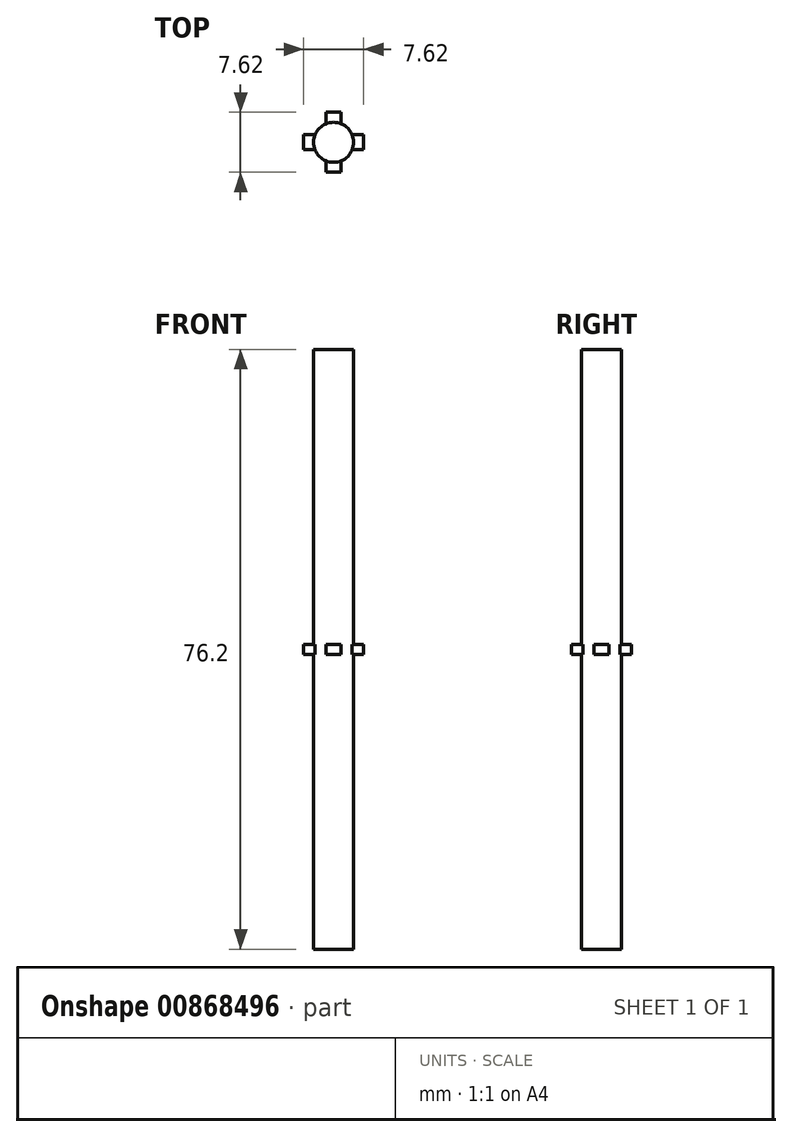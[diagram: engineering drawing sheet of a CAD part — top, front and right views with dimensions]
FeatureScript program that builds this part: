
annotation { "Feature Type Name" : "Feature", "Feature Type Description" : "" }
export const myFeature = defineFeature(function(context is Context, id is Id, definition is map)
    precondition{}
    {
        {
            var Q0;
            Q0=qCreatedBy(makeId("Top.planeOp"),FACE);
            var sketch = newSketch(context, id + "F0", { "sketchPlane" : qUnion([Q0])});
            skCircle(sketch, "E0", {"center": v(0, 0) * mm, "radius": 2.54 * mm});
            skSolve(sketch);
        }
        {
            var Q0;
            Q0 = qSketchRegion(id + "F0", true);
            extrude(context, id + "F1", {"entities" : qUnion([Q0]), "depth" : 76.2 * mm, "offsetDistance" : 25.4 * mm});
        }
        {
            var Q0;
            Q0=qCreatedBy(makeId("Top.planeOp"),FACE);
            cPlane(context, id + "F2", {"entities" : qUnion([Q0]), "cplaneType" : CPlaneType.OFFSET, "offset" : 38.1 * mm, "width" : 152.4 * mm, "height" : 152.4 * mm});
        }
        {
            var Q0;
            Q0=qCreatedBy(id+"F2.planeOp",FACE);
            var sketch = newSketch(context, id + "F3", { "sketchPlane" : qUnion([Q0])});
            skLineSegment(sketch, "E1.bottom", {"start": v(0.95, 3.81) * mm, "end": v(-0.95, 3.81) * mm});
            skLineSegment(sketch, "E1.top", {"start": v(0.95, -3.81) * mm, "end": v(-0.95, -3.81) * mm});
            skLineSegment(sketch, "E1.left", {"start": v(0.95, 3.81) * mm, "end": v(0.95, 0.95) * mm});
            skLineSegment(sketch, "E1.right", {"start": v(-0.95, 3.81) * mm, "end": v(-0.95, 0.95) * mm});
            skLineSegment(sketch, "E2.bottom", {"start": v(3.81, 0.95) * mm, "end": v(0.95, 0.95) * mm});
            skLineSegment(sketch, "E2.top", {"start": v(3.81, -0.95) * mm, "end": v(0.95, -0.95) * mm});
            skLineSegment(sketch, "E2.left", {"start": v(3.81, 0.95) * mm, "end": v(3.81, -0.95) * mm});
            skLineSegment(sketch, "E2.right", {"start": v(-3.8, 0.95) * mm, "end": v(-3.8, -0.95) * mm});
            skLineSegment(sketch, "E3.trimOffspring", {"start": v(0.95, -0.95) * mm, "end": v(0.95, -3.81) * mm});
            skLineSegment(sketch, "E4.trimOffspring", {"start": v(-0.95, 0.95) * mm, "end": v(-3.8, 0.95) * mm});
            skLineSegment(sketch, "E5.trimOffspring", {"start": v(-0.95, -0.95) * mm, "end": v(-0.95, -3.81) * mm});
            skLineSegment(sketch, "E6.trimOffspring", {"start": v(-0.95, -0.95) * mm, "end": v(-3.8, -0.95) * mm});
            skSolve(sketch);
        }
        {
            var Q0;
            Q0 = qSketchRegion(id + "F3", true);
            extrude(context, id + "F4", {"entities" : qUnion([Q0]), "operationType" : NewBodyOperationType.ADD, "endBound" : BoundingType.SYMMETRIC, "depth" : 1.27 * mm, "offsetDistance" : 25.4 * mm});
        }
    });
